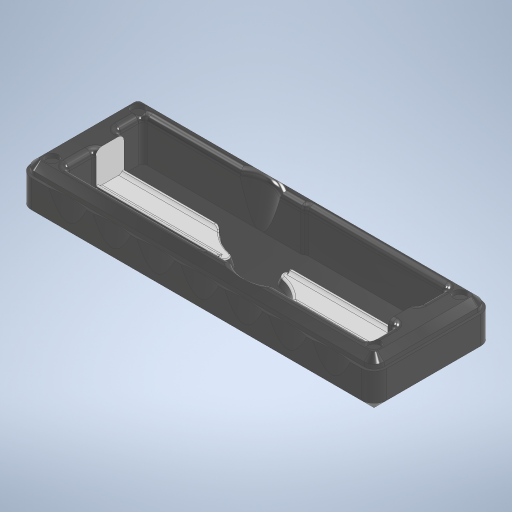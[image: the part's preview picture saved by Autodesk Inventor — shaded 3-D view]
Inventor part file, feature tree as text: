
AUTODESK INVENTOR PART (.ipt)
format: ipt  version: 2024.1 (Build 281209000, 209)  size: 910,848 bytes
history: native  units: mm
features: fillet x7, other x4, extrude x3, sketch x3
ambient origin geometry x8: Origin, YZ Plane, XZ Plane, XY Plane, X Axis, Y Axis, Z Axis, Center Point
bodies: Body1 (feature_tree)
feature tree (17):
  other  "pen-case.ipt"
  extrude  "Extrusion1"  Depth=138.0mm
  extrude  "Extrusion2"  Depth=0.5mm
  fillet  "Fillet1"  Radius=12.8mm
  fillet  "Fillet2"  Radius=0.4mm
  extrude  "Extrusion3"  Depth=15.8mm TaperAngle=0.0deg
  fillet  "Fillet5"  Radius=0.55mm
  fillet  "Fillet6"  Radius=0.55mm
  fillet  "Fillet7"  Radius=0.55mm
  fillet  "Fillet3"  Radius=2.0mm
  fillet  "Fillet4"  Radius=2.0mm
  other  "case::pen-case.ipt"
  other  "TaggingFeature1"
  sketch  "Sketch1"  dims[d0=10.0mm d1=138.0mm]
  sketch  "Sketch2"  dims[d2=0.5mm d3=0.5mm d4=12.8mm d5=0.4mm]
  sketch  "Sketch3"  dims[d6=0.4mm d7=15.8mm d8=0.0mm d9=0.55mm d10=0.55mm d11=0.55mm d12=2.0mm d13=0.0mm d14=2.0mm d15=0.5mm d16=14.0mm d17=0.0mm d18=2.0mm d19=2.0mm d20=0.5mm d21=1.0mm d22=0.5mm]
  other  "case"
